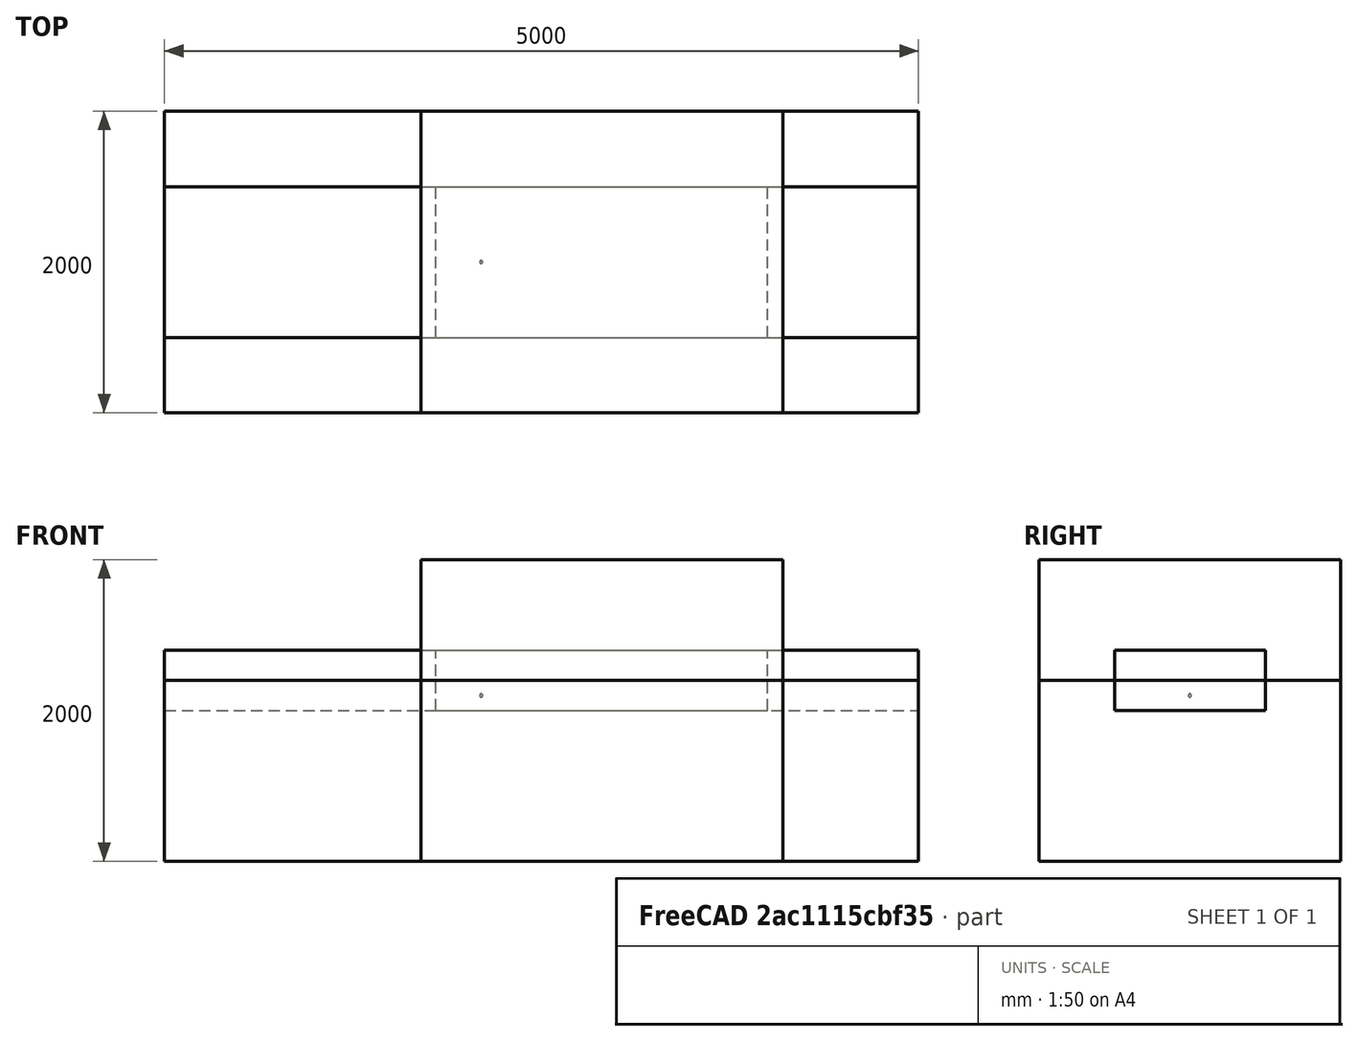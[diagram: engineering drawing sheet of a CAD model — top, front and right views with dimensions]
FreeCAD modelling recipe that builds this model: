
FCSTD DOCUMENT  (FreeCAD 0.18.1R)
Label: DSPH_Case
License: All rights reserved
LicenseURL: http://en.wikipedia.org/wiki/All_rights_reserved
objects: Part::Box×5, Part::Sphere×1, App::DocumentObjectGroup×1, Mesh::Feature×1
note: 6 computed .brp shape members not serialized (recipe doc carries the construction recipe); baked Part::Feature solids carry a one-line shape summary decoded from their .brp

FEATURE [Part::Box] Case_Limits  label="Case Limits (3D)"
  AttacherType = Attacher::AttachEngine3D
  Height = 2000
  Length = 2400
  Placement = pos=(-300,-1000,-1000) rot=(0,0,1;0rad)
  Width = 2000
FEATURE [Part::Box] Box  label="LeftFill"
  AttacherType = Attacher::AttachEngine3D
  Height = 400
  Length = 2200
  Placement = pos=(-200,-500,0) rot=(0,0,1;0rad)
  Width = 1000
FEATURE [Part::Box] Box001  label="RightFill"
  AttacherType = Attacher::AttachEngine3D
  Height = 400
  Length = 2200
  Placement = pos=(-200,-500,0) rot=(0,0,1;0rad)
  Width = 1000
FEATURE [Part::Box] Box002  label="Walls"
  AttacherType = Attacher::AttachEngine3D
  Height = 400
  Length = 5000
  Placement = pos=(-2000,-500,0) rot=(0,0,1;0rad)
  Width = 1000
FEATURE [Part::Sphere] FillPoint
  Angle1 = -90
  Angle2 = 90
  Angle3 = 360
  AttacherType = Attacher::AttachEngine3D
  Placement = pos=(100,0,100) rot=(0,0,1;0rad)
  Radius = 10
FEATURE [Part::Box] FillLimit
  AttacherType = Attacher::AttachEngine3D
  Height = 1200
  Length = 5000
  Placement = pos=(-2000,-1000,-1000) rot=(0,0,1;0rad)
  Width = 2000
FEATURE [App::DocumentObjectGroup] FillBox
  Group = -> [FillLimit,FillPoint]
FEATURE [Mesh::Feature] ARC
  Placement = pos=(155,209,-36) rot=(0,0,1;0rad)
